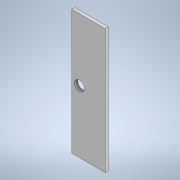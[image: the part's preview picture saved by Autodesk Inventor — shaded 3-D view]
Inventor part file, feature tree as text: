
AUTODESK INVENTOR PART (.ipt)
format: ipt  version: 2021 (Build 250183000, 183)  size: 118,272 bytes
history: native  units: mm
features: extrude x3, sketch x3
ambient origin geometry x8: Origin, YZ Plane, XZ Plane, XY Plane, X Axis, Y Axis, Z Axis, Center Point
bodies: Solid1 (feature_tree)
feature tree (6):
  extrude  "Extrusion1"  Depth=86.0mm
  extrude  "Extrusion2"  Depth=11.0mm
  extrude  "Extrusion3"  Depth=2.0mm
  sketch  "Sketch1"  dims[d0=24.0mm d1=86.0mm]
  sketch  "Sketch2"  dims[d2=43.0mm d3=11.0mm]
  sketch  "Sketch3"  dims[d4=2.0mm d5=0.0mm d6=6.5mm d7=18.8mm d8=2.0mm d9=0.0mm d10=2.0mm d11=2.0mm d12=2.0mm d13=2.0mm d14=0.0mm]
